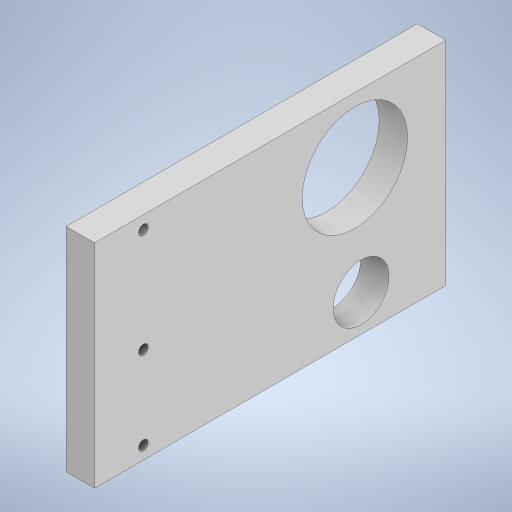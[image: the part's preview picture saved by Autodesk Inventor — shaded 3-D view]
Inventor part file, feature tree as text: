
AUTODESK INVENTOR PART (.ipt)
format: ipt  version: 2023 (Build 270158000, 158)  size: 225,280 bytes
history: native  units: in
note: dims shown in document units (in); Inventor stores cm internally (conversion verified against a paired STEP export)
features: extrude x1
ambient origin geometry x8: Origin, YZ Plane, XZ Plane, XY Plane, X Axis, Y Axis, Z Axis, Center Point
bodies: Body1 (feature_tree)
feature tree (1):
  extrude  "Extrusion6"  Depth=0.15in
